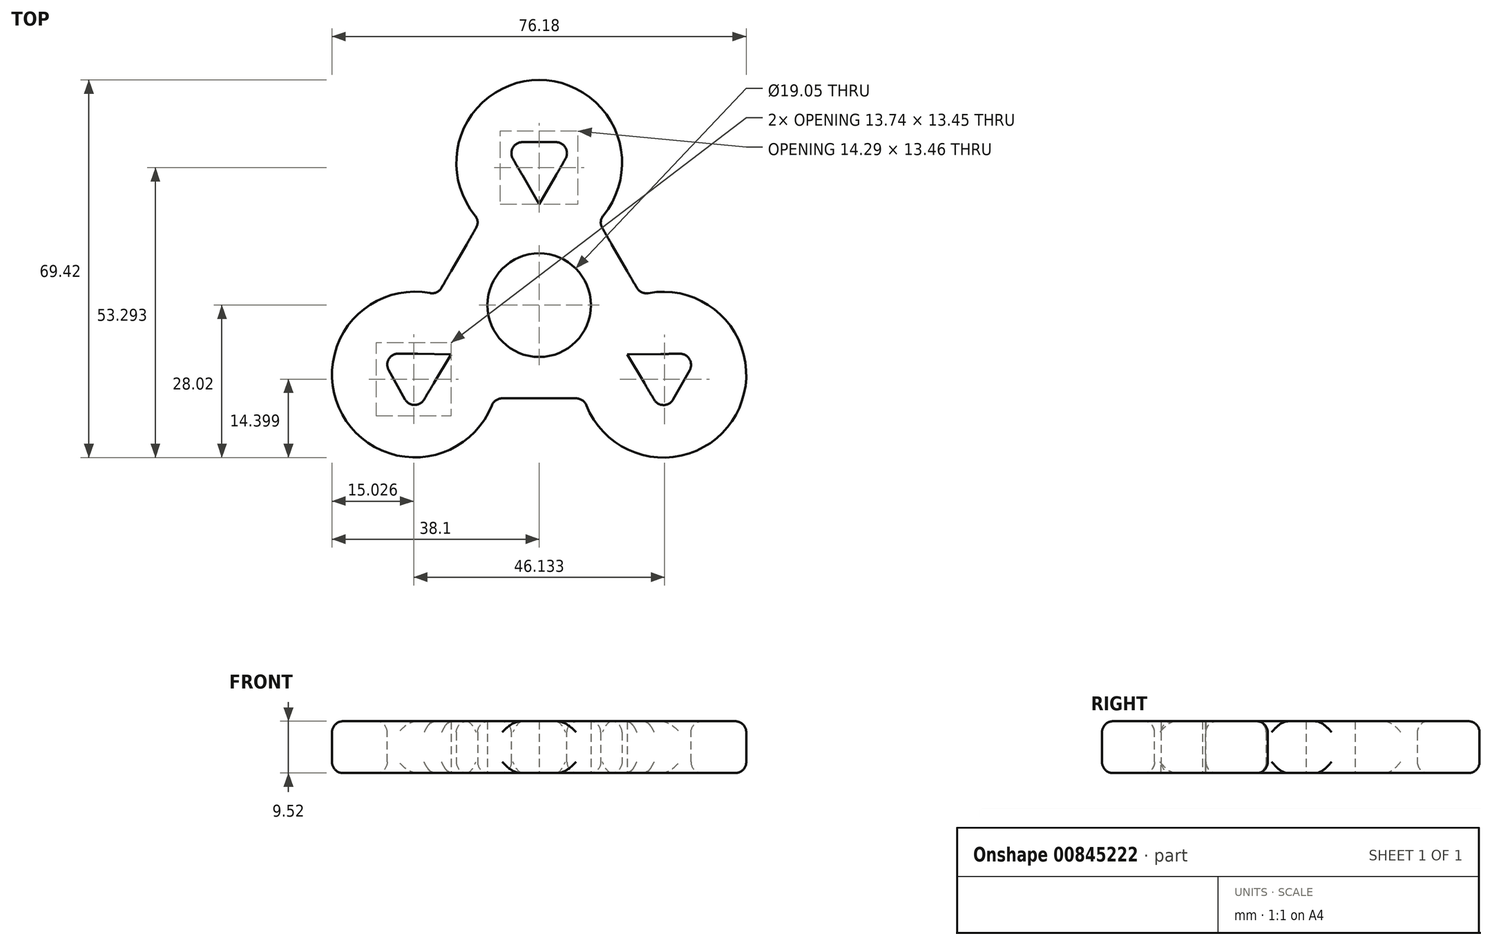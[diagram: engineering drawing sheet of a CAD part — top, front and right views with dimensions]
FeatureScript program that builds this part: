
annotation { "Feature Type Name" : "Feature", "Feature Type Description" : "" }
export const myFeature = defineFeature(function(context is Context, id is Id, definition is map)
    precondition{}
    {
        {
            var Q0;
            Q0=qCreatedBy(makeId("Top.planeOp"),FACE);
            var sketch = newSketch(context, id + "F0", { "sketchPlane" : qUnion([Q0])});
            skCircle(sketch, "E0.cCircle", {"center": v(0, 0) * mm, "radius": 34.3 * mm, "construction": true});
            skLineSegment(sketch, "E0.0", {"start": v(10.86, 15.47) * mm, "end": v(18.7, 1.89) * mm});
            skLineSegment(sketch, "E0.1", {"start": v(8.24, -17.14) * mm, "end": v(-8.26, -17.15) * mm});
            skLineSegment(sketch, "E0.2", {"start": v(-18.7, 1.9) * mm, "end": v(-10.86, 15.47) * mm});
            skArc(sketch, "E1", {"start": v(10.86, 15.47) * mm, "mid": v(0, 41.4) * mm, "end": v(-10.86, 15.47) * mm});
            skArc(sketch, "E2", {"start": v(-18.7, 1.9) * mm, "mid": v(-36.22, -20.07) * mm, "end": v(-8.26, -17.15) * mm});
            skArc(sketch, "E3", {"start": v(8.24, -17.15) * mm, "mid": v(36.2, -20.13) * mm, "end": v(18.7, 1.89) * mm});
            skCircle(sketch, "E4", {"center": v(0, 0) * mm, "radius": 9.53 * mm});
            skPoint(sketch, "E5.orphan", {"position": v(0, 34.3) * mm});
            skPoint(sketch, "E6.orphan", {"position": v(29.7, -17.14) * mm});
            skPoint(sketch, "E7.orphan", {"position": v(-29.7, -17.15) * mm});
            skLineSegment(sketch, "E8", {"start": v(0, 9.53) * mm, "end": v(0, 18.54) * mm});
            skCircle(sketch, "E9.cCircle", {"center": v(0, 26.16) * mm, "radius": 7.62 * mm, "construction": true});
            skLineSegment(sketch, "E9.0", {"start": v(0, 18.54) * mm, "end": v(-6.6, 29.97) * mm});
            skLineSegment(sketch, "E9.1", {"start": v(-6.6, 29.97) * mm, "end": v(6.6, 29.97) * mm});
            skLineSegment(sketch, "E9.2", {"start": v(6.6, 29.97) * mm, "end": v(0, 18.54) * mm});
            skCircle(sketch, "E10.cCircle", {"center": v(22.84, -12.78) * mm, "radius": 7.62 * mm, "construction": true});
            skLineSegment(sketch, "E10.0", {"start": v(16.19, -9.06) * mm, "end": v(29.39, -8.88) * mm});
            skLineSegment(sketch, "E10.1", {"start": v(29.39, -8.88) * mm, "end": v(22.94, -20.4) * mm});
            skLineSegment(sketch, "E10.2", {"start": v(22.94, -20.4) * mm, "end": v(16.19, -9.06) * mm});
            skCircle(sketch, "E11.cCircle", {"center": v(-22.86, -12.75) * mm, "radius": 7.62 * mm, "construction": true});
            skLineSegment(sketch, "E11.0", {"start": v(-16.2, -9.04) * mm, "end": v(-22.97, -20.37) * mm});
            skLineSegment(sketch, "E11.1", {"start": v(-22.97, -20.37) * mm, "end": v(-29.4, -8.85) * mm});
            skLineSegment(sketch, "E11.2", {"start": v(-29.4, -8.85) * mm, "end": v(-16.2, -9.04) * mm});
            skSolve(sketch);
        }
        {
            var Q0;
            Q0 = qSketchRegion(id + "F0", true);
            extrude(context, id + "F1", {"entities" : qUnion([Q0]), "endBound" : BoundingType.SYMMETRIC, "depth" : 9.52 * mm, "offsetDistance" : 25.4 * mm});
        }
        {
            var Q0;
            Q0=makeQuery(id+"F1.opExtrude","SWEPT_FACE",FACE,{"disambiguationData":[OSD([sQuery(id+"F0.wireOp",EDGE,"E1")])]});
            var Q1;
            Q1=makeQuery(id+"F1.opExtrude","SWEPT_FACE",FACE,{"disambiguationData":[OSD([sQuery(id+"F0.wireOp",EDGE,"E2")])]});
            var Q2;
            Q2=makeQuery(id+"F1.opExtrude","SWEPT_FACE",FACE,{"disambiguationData":[OSD([sQuery(id+"F0.wireOp",EDGE,"E3")])]});
            var Q3;
            Q3=makeQuery(id+"F1.opExtrude","SWEPT_FACE",FACE,{"disambiguationData":[OSD([sQuery(id+"F0.wireOp",EDGE,"E11.1")])]});
            var Q4;
            Q4=makeQuery(id+"F1.opExtrude","SWEPT_FACE",FACE,{"disambiguationData":[OSD([sQuery(id+"F0.wireOp",EDGE,"E9.1")])]});
            var Q5;
            Q5=makeQuery(id+"F1.opExtrude","SWEPT_FACE",FACE,{"disambiguationData":[OSD([sQuery(id+"F0.wireOp",EDGE,"E10.1")])]});
            fillet(context, id + "F2", {"entities" : qUnion([Q0, Q1, Q2, Q3, Q4, Q5]), "radius" : 2.03 * mm, "tangentPropagation" : true, "allowEdgeOverflow" : false});
        }
    });
